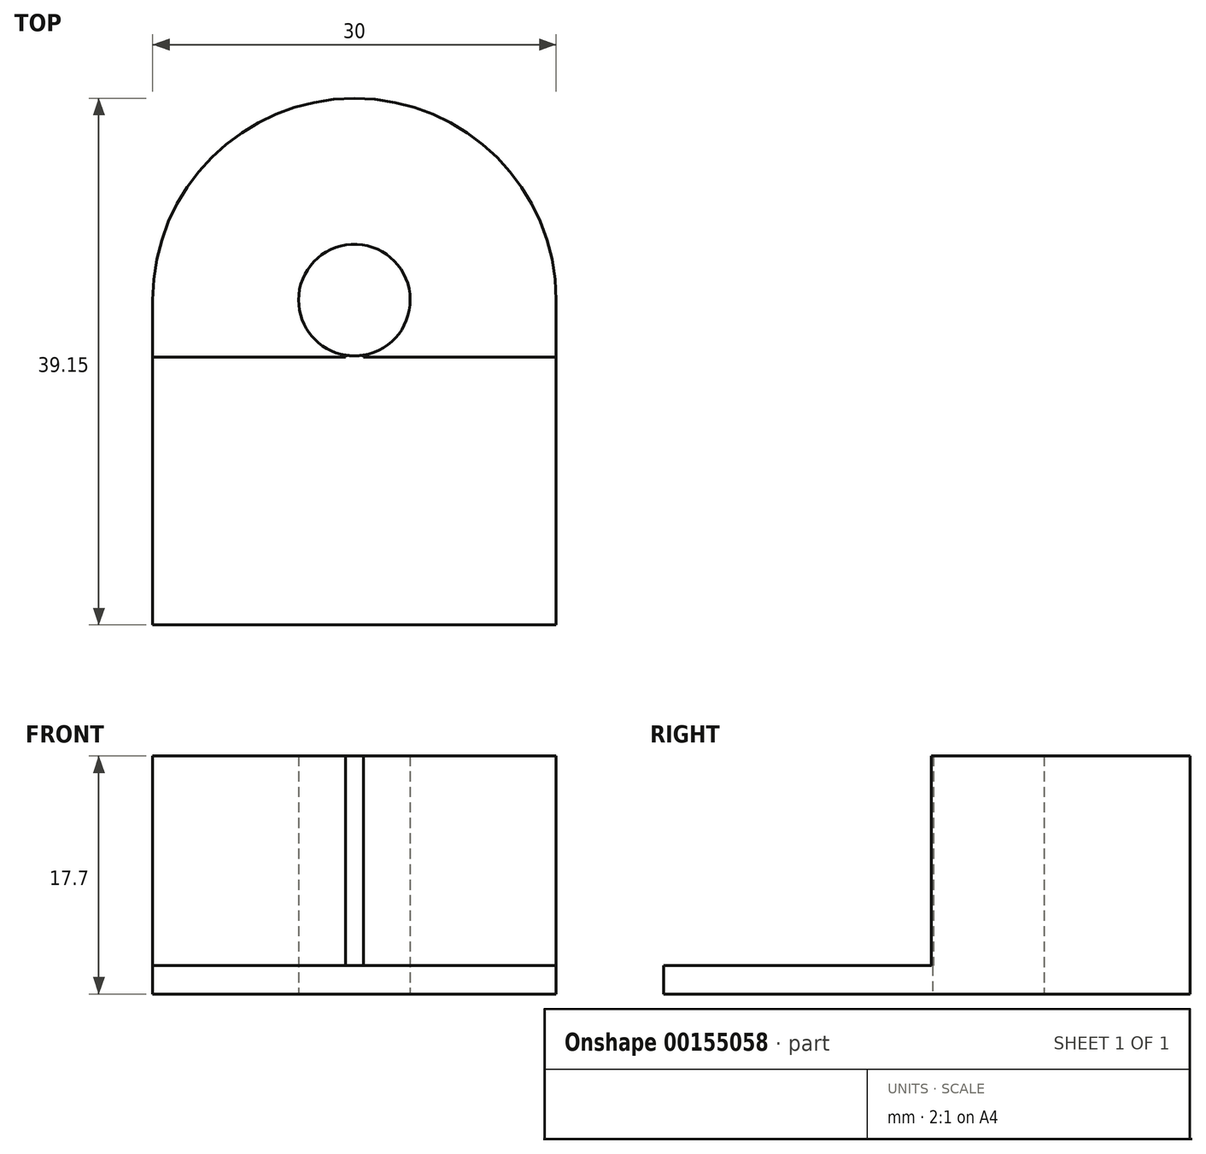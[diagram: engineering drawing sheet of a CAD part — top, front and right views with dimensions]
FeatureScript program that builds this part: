
annotation { "Feature Type Name" : "Feature", "Feature Type Description" : "" }
export const myFeature = defineFeature(function(context is Context, id is Id, definition is map)
    precondition{}
    {
        {
            var Q0;
            Q0=qCreatedBy(makeId("Top.planeOp"),FACE);
            var sketch = newSketch(context, id + "F0", { "sketchPlane" : qUnion([Q0])});
            skArc(sketch, "E0", {"start": v(0.66, -4.1) * mm, "mid": v(0, 4.15) * mm, "end": v(-0.66, -4.1) * mm});
            skArc(sketch, "E1", {"start": v(15, 0) * mm, "mid": v(0, 15) * mm, "end": v(-15, 0) * mm});
            skLineSegment(sketch, "E2", {"start": v(-15, -4.25) * mm, "end": v(-0.66, -4.25) * mm});
            skLineSegment(sketch, "E3", {"start": v(-15, 0) * mm, "end": v(-15, -4.25) * mm});
            skLineSegment(sketch, "E4", {"start": v(15, 0) * mm, "end": v(15, -4.25) * mm});
            skLineSegment(sketch, "E5", {"start": v(-0.66, -4.25) * mm, "end": v(-0.66, -4.1) * mm});
            skLineSegment(sketch, "E6", {"start": v(0.66, -4.25) * mm, "end": v(0.66, -4.1) * mm});
            skPoint(sketch, "E7", {"position": v(0, -4.25) * mm});
            skLineSegment(sketch, "E8.trimOffspring", {"start": v(0.66, -4.25) * mm, "end": v(15, -4.25) * mm});
            skSolve(sketch);
        }
        {
            var Q0;
            Q0 = qSketchRegion(id + "F0", true);
            extrude(context, id + "F1", {"entities" : qUnion([Q0]), "depth" : 15.6 * mm});
        }
        {
            var Q0;
            Q0=makeQuery(id+"F1.opExtrude","CAP_FACE",FACE,{"disambiguationData":[OSD([sQuery(id+"F0.wireOp",EDGE,"E0"),sQuery(id+"F0.wireOp",EDGE,"E1"),sQuery(id+"F0.wireOp",EDGE,"E2"),sQuery(id+"F0.wireOp",EDGE,"E3"),sQuery(id+"F0.wireOp",EDGE,"E4")])],"isStart":true});
            var sketch = newSketch(context, id + "F2", { "sketchPlane" : qUnion([Q0])});
            skCircle(sketch, "E9.0", {"center": v(0, 0) * mm, "radius": 4.15 * mm});
            skArc(sketch, "E10.0", {"start": v(15, 0) * mm, "mid": v(0, -15) * mm, "end": v(-15, 0) * mm});
            skLineSegment(sketch, "E11.0", {"start": v(-15, 0) * mm, "end": v(-15, 24.15) * mm});
            skLineSegment(sketch, "E12.0", {"start": v(15, 0) * mm, "end": v(15, 24.15) * mm});
            skLineSegment(sketch, "E13", {"start": v(15, 24.15) * mm, "end": v(-15, 24.15) * mm});
            skSolve(sketch);
        }
        {
            var Q0;
            Q0 = qSketchRegion(id + "F2", true);
            extrude(context, id + "F3", {"entities" : qUnion([Q0]), "operationType" : NewBodyOperationType.ADD, "depth" : 2.1 * mm});
        }
    });
